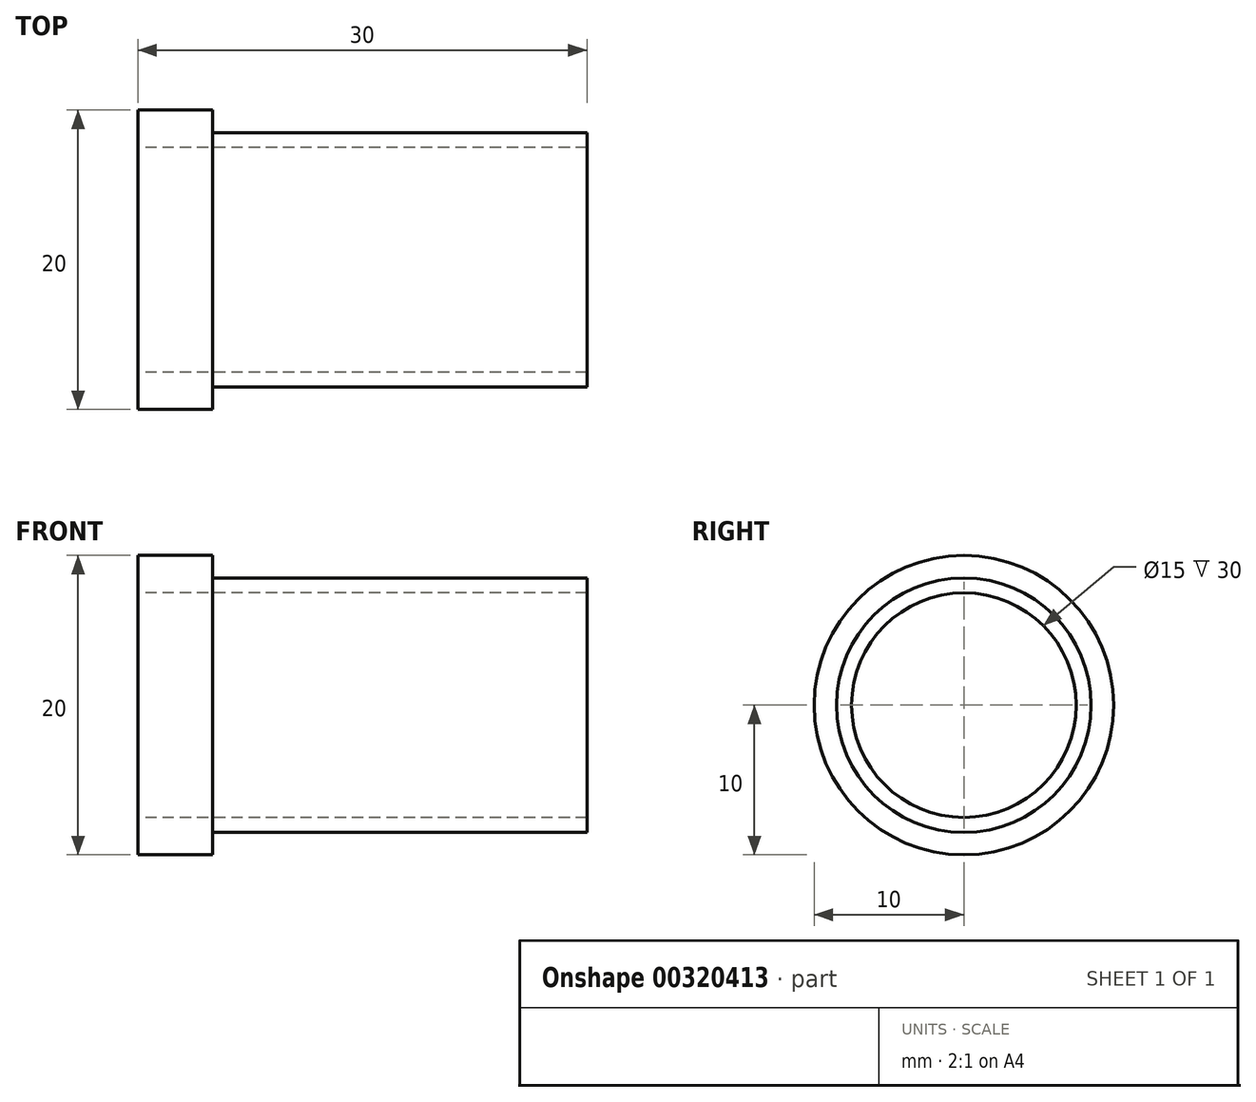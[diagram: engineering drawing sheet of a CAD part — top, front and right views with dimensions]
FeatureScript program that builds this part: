
annotation { "Feature Type Name" : "Feature", "Feature Type Description" : "" }
export const myFeature = defineFeature(function(context is Context, id is Id, definition is map)
    precondition{}
    {
        {
            var Q0;
            Q0=qCreatedBy(makeId("Front.planeOp"),FACE);
            var sketch = newSketch(context, id + "F0", { "sketchPlane" : qUnion([Q0])});
            skLineSegment(sketch, "E0", {"start": v(-21.08, 0) * mm, "end": v(23.9, 0) * mm});
            skSolve(sketch);
        }
        {
            var Q0;
            Q0=qCreatedBy(makeId("Front.planeOp"),FACE);
            var sketch = newSketch(context, id + "F1", { "sketchPlane" : qUnion([Q0])});
            skLineSegment(sketch, "E1", {"start": v(-9.27, 10) * mm, "end": v(-9.27, 8.5) * mm});
            skLineSegment(sketch, "E2", {"start": v(15.73, 8.5) * mm, "end": v(-9.27, 8.5) * mm});
            skLineSegment(sketch, "E3", {"start": v(-9.27, 10) * mm, "end": v(-14.27, 10) * mm});
            skLineSegment(sketch, "E4", {"start": v(-14.27, 7.5) * mm, "end": v(15.73, 7.5) * mm});
            skLineSegment(sketch, "E5", {"start": v(-14.27, 10) * mm, "end": v(-14.27, 7.5) * mm});
            skLineSegment(sketch, "E6", {"start": v(15.73, 8.5) * mm, "end": v(15.73, 7.5) * mm});
            skSolve(sketch);
        }
        {
            var Q0;
            Q0=makeQuery(id+"F1.imprint","IMPRINT",FACE,{"disambiguationData":[TD([[makeQuery(id+"F1.imprint","IMPRINT",EDGE,{"derivedFrom":sQuery(id+"F1.wireOp",EDGE,"E1")}),-1.0]])]});
            var Q1;
            Q1=sQuery(id+"F0.wireOp",EDGE,"E0");
            revolve(context, id + "F2", {"entities" : qUnion([Q0]), "axis" : qUnion([Q1]), "revolveType" : RevolveType.FULL});
        }
    });
